# Revit family: Duct_Door-Acudor-Round-RD-5090_Series
name_source: partatom
category: Specialty Equipment
revit_build: Autodesk Revit 2014 (Build: 20130308_1515(x64)
units: mm (PartAtom-declared; Revit-internal decimal feet)

## types (9) — shared parameters
Assembly Code = C1020700
Default Elevation = 0"
Description = Round Duct Access Door
Finish = Galvanized Steel-Acudor-16 Gauge-Mill Finish
Installation Type = Surface Mount
Manufacturer = Acudor
Material = Galvanized Steel-Acudor-16 Gauge-Mill Finish
Product Documentation Link = https://acudor.com
Product Page URL = https://acudor.com
URL = http://acudor.com

## per-type parameters (varying)
| type | Duct Diameter | Duct Radius | Latch Distance | Outer Duct Diameter | Outer Duct Radius | Width |
| RD-5090 7x5 | 6" | 3" | 1 3/8" | 6 1/8" | 3 1/16" | 7" |
| RD-5090 9x8 | 8" | 4" | 1 1/8" | 8 1/8" | 4 1/16" | 9" |
| RD-5090 11x9 | 10" | 5" | 15/16" | 10 1/8" | 5 1/16" | 11" |
| RD-5090 13x10 | 12" | 6" | 7/8" | 12 1/8" | 6 1/16" | 13" |
| RD-5090 15x13 | 14" | 7" | 3/4" | 14 1/8" | 7 1/16" | 15" |
| RD-5090 17x13 | 16" | 8" | 11/16" | 16 1/8" | 8 1/16" | 17" |
| RD-5090 19x15 | 18" | 9" | 5/8" | 18 1/8" | 9 1/16" | 19" |
| RD-5090 19x17 | 20" | 10" | 1/2" | 20 1/8" | 10 1/16" | 19" |
| RD-5090 20x17 | 24" | 12" | 3/8" | 24 1/8" | 12 1/16" | 20" |

note: column(s) folded — value = type name in every type: Model

## geometry (parser evidence)
native form markers: Sweep x3
no freeform markers — native parametric forms only
